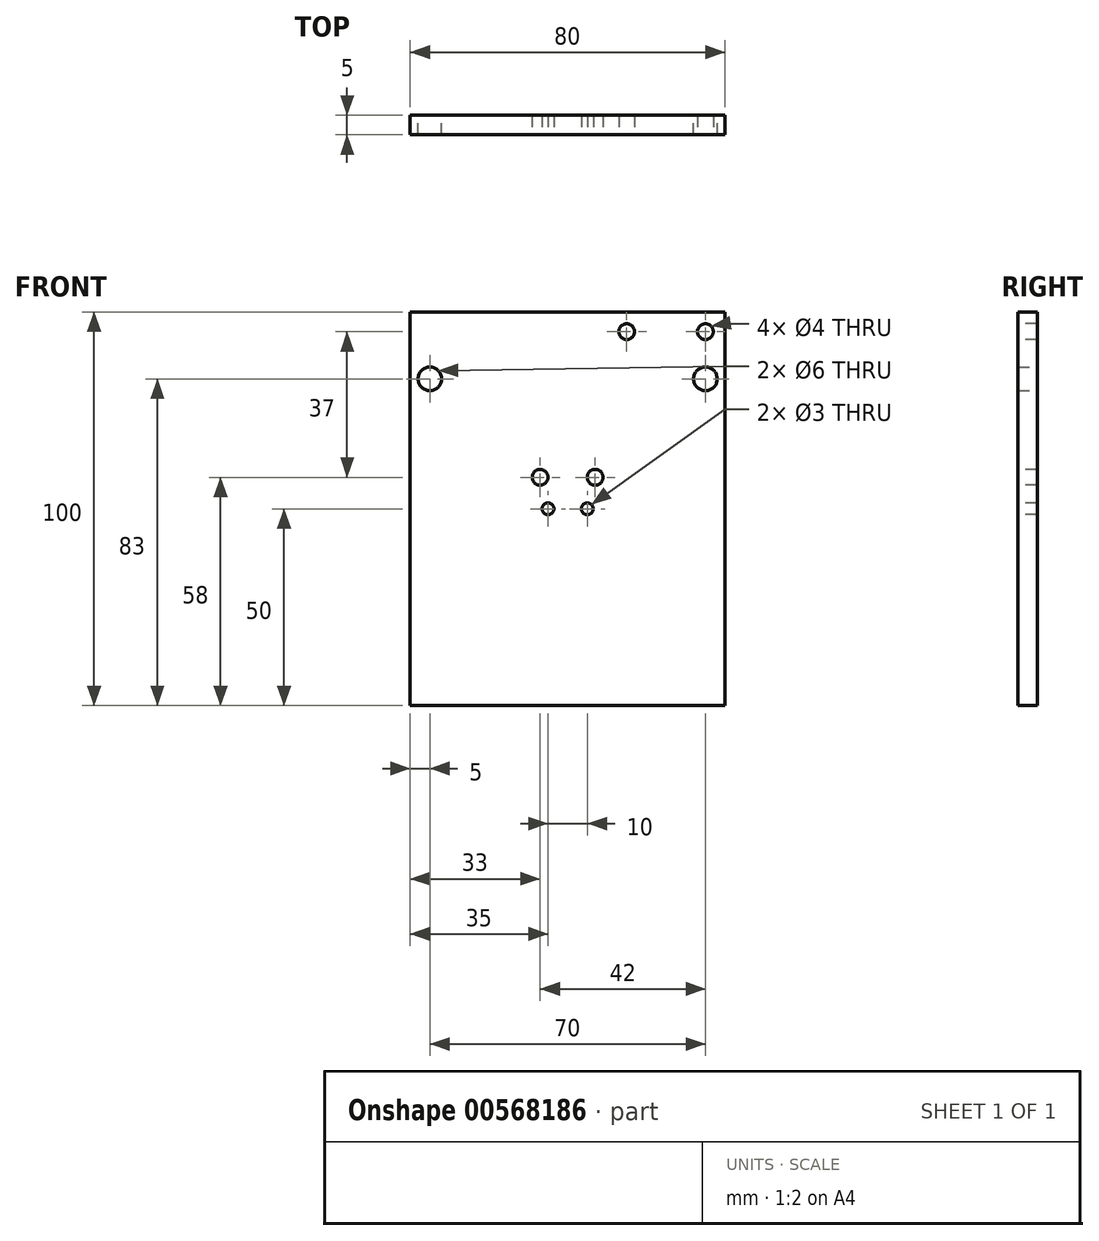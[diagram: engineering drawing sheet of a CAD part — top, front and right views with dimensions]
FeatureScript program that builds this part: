
annotation { "Feature Type Name" : "Feature", "Feature Type Description" : "" }
export const myFeature = defineFeature(function(context is Context, id is Id, definition is map)
    precondition{}
    {
        {
            var Q0;
            Q0=qCreatedBy(makeId("Top.planeOp"),FACE);
            var sketch = newSketch(context, id + "F0", { "sketchPlane" : qUnion([Q0])});
            skLineSegment(sketch, "E0.bottom", {"start": v(0, 0) * mm, "end": v(80, 0) * mm});
            skLineSegment(sketch, "E0.top", {"start": v(0, 5) * mm, "end": v(80, 5) * mm});
            skLineSegment(sketch, "E0.left", {"start": v(0, 0) * mm, "end": v(0, 5) * mm});
            skLineSegment(sketch, "E0.right", {"start": v(80, 0) * mm, "end": v(80, 5) * mm});
            skSolve(sketch);
        }
        {
            var Q0;
            Q0 = qSketchRegion(id + "F0", true);
            extrude(context, id + "F1", {"entities" : qUnion([Q0]), "depth" : 100 * mm, "offsetDistance" : 25 * mm});
        }
        {
            var Q0;
            Q0=makeQuery(id+"F1.opExtrude","SWEPT_FACE",FACE,{"disambiguationData":[OSD([sQuery(id+"F0.wireOp",EDGE,"E0.top")])]});
            var sketch = newSketch(context, id + "F2", { "sketchPlane" : qUnion([Q0])});
            skLineSegment(sketch, "E1", {"start": v(-70, 83) * mm, "end": v(-80, 83) * mm, "construction": true});
            skCircle(sketch, "E2", {"center": v(-5, 83) * mm, "radius": 3 * mm});
            skCircle(sketch, "E3", {"center": v(-75, 83) * mm, "radius": 3 * mm});
            skSolve(sketch);
        }
        {
            var Q0;
            Q0 = qSketchRegion(id + "F2", true);
            extrude(context, id + "F3", {"entities" : qUnion([Q0]), "operationType" : NewBodyOperationType.REMOVE, "oppositeDirection" : true, "depth" : 25 * mm, "offsetDistance" : 25 * mm});
        }
        {
            var Q0;
            Q0=makeQuery(id+"F1.opExtrude","SWEPT_FACE",FACE,{"disambiguationData":[OSD([sQuery(id+"F0.wireOp",EDGE,"E0.bottom")])]});
            var sketch = newSketch(context, id + "F4", { "sketchPlane" : qUnion([Q0])});
            skLineSegment(sketch, "E4", {"start": v(40, 0) * mm, "end": v(40, 100) * mm, "construction": true});
            skLineSegment(sketch, "E5", {"start": v(0, 50) * mm, "end": v(80, 50) * mm, "construction": true});
            skCircle(sketch, "E6", {"center": v(45, 50) * mm, "radius": 1.5 * mm});
            skCircle(sketch, "E7", {"center": v(35, 50) * mm, "radius": 1.5 * mm});
            skSolve(sketch);
        }
        {
            var Q0;
            Q0 = qSketchRegion(id + "F4", true);
            extrude(context, id + "F5", {"entities" : qUnion([Q0]), "operationType" : NewBodyOperationType.REMOVE, "oppositeDirection" : true, "depth" : 25 * mm, "offsetDistance" : 25 * mm});
        }
        {
            var Q0;
            Q0=makeQuery(id+"F1.opExtrude","SWEPT_FACE",FACE,{"disambiguationData":[OSD([sQuery(id+"F0.wireOp",EDGE,"E0.bottom")])]});
            var sketch = newSketch(context, id + "F6", { "sketchPlane" : qUnion([Q0])});
            skLineSegment(sketch, "E8", {"start": v(80, 95) * mm, "end": v(0, 95) * mm, "construction": true});
            skCircle(sketch, "E9", {"center": v(75, 95) * mm, "radius": 2 * mm});
            skCircle(sketch, "E10", {"center": v(55, 95) * mm, "radius": 2 * mm});
            skSolve(sketch);
        }
        {
            var Q0;
            Q0 = qSketchRegion(id + "F6", true);
            extrude(context, id + "F7", {"entities" : qUnion([Q0]), "operationType" : NewBodyOperationType.REMOVE, "oppositeDirection" : true, "depth" : 25 * mm, "offsetDistance" : 25 * mm});
        }
        {
            var Q0;
            Q0=makeQuery(id+"F1.opExtrude","SWEPT_FACE",FACE,{"disambiguationData":[OSD([sQuery(id+"F0.wireOp",EDGE,"E0.bottom")])]});
            var sketch = newSketch(context, id + "F8", { "sketchPlane" : qUnion([Q0])});
            skLineSegment(sketch, "E11", {"start": v(40, 100) * mm, "end": v(40, 0) * mm, "construction": true});
            skLineSegment(sketch, "E12", {"start": v(0, 58) * mm, "end": v(80, 58) * mm, "construction": true});
            skCircle(sketch, "E13", {"center": v(33, 58) * mm, "radius": 2 * mm});
            skCircle(sketch, "E14", {"center": v(47, 58) * mm, "radius": 2 * mm});
            skSolve(sketch);
        }
        {
            var Q0;
            Q0 = qSketchRegion(id + "F8", true);
            extrude(context, id + "F9", {"entities" : qUnion([Q0]), "operationType" : NewBodyOperationType.REMOVE, "oppositeDirection" : true, "depth" : 25 * mm, "offsetDistance" : 25 * mm});
        }
    });
